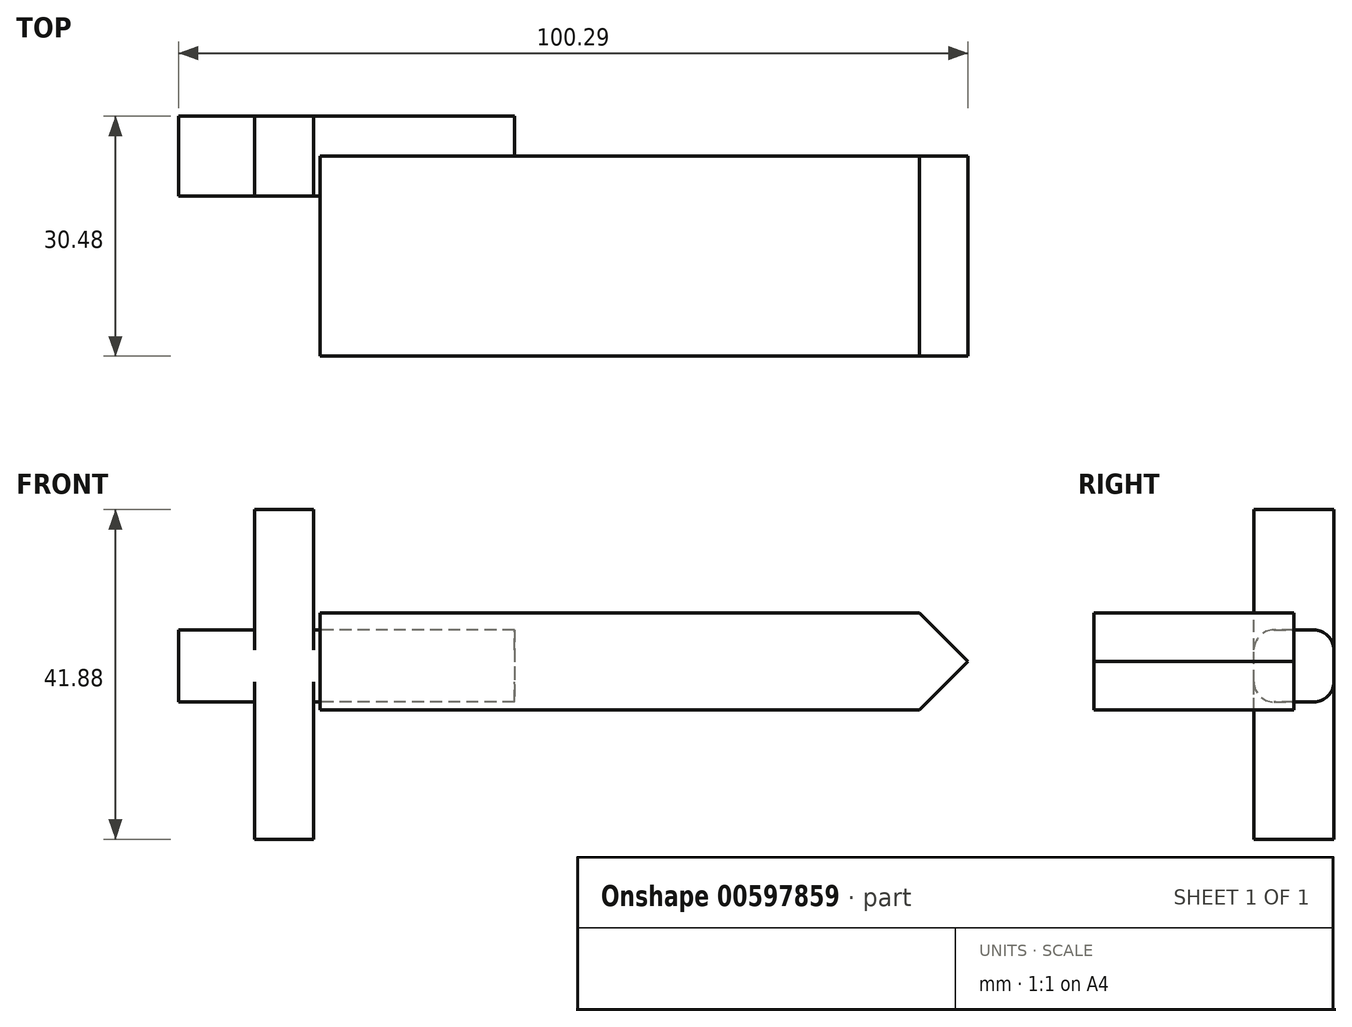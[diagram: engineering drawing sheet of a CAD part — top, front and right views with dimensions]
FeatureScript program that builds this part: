
annotation { "Feature Type Name" : "Feature", "Feature Type Description" : "" }
export const myFeature = defineFeature(function(context is Context, id is Id, definition is map)
    precondition{}
    {
        {
            var Q0;
            Q0=qCreatedBy(makeId("Front.planeOp"),FACE);
            var sketch = newSketch(context, id + "F0", { "sketchPlane" : qUnion([Q0])});
            skLineSegment(sketch, "E0.bottom", {"start": v(-28.06, 29.4) * mm, "end": v(-94.64, 29.4) * mm});
            skLineSegment(sketch, "E0.top", {"start": v(-28.06, 38.53) * mm, "end": v(-94.64, 38.53) * mm});
            skLineSegment(sketch, "E0.left", {"start": v(-28.06, 29.4) * mm, "end": v(-28.06, 38.53) * mm});
            skLineSegment(sketch, "E0.right", {"start": v(-94.64, 29.4) * mm, "end": v(-94.64, 38.53) * mm});
            skPoint(sketch, "E0.middle", {"position": v(-61.35, 33.96) * mm});
            skLineSegment(sketch, "E1.bottom", {"start": v(-84.98, 11.95) * mm, "end": v(-77.46, 11.95) * mm});
            skLineSegment(sketch, "E1.top", {"start": v(-84.98, 53.83) * mm, "end": v(-77.46, 53.83) * mm});
            skLineSegment(sketch, "E1.left", {"start": v(-84.98, 11.95) * mm, "end": v(-84.98, 53.83) * mm});
            skLineSegment(sketch, "E1.right", {"start": v(-77.46, 11.95) * mm, "end": v(-77.46, 53.83) * mm});
            skPoint(sketch, "E1.middle", {"position": v(-81.22, 32.9) * mm});
            skLineSegment(sketch, "E2.bottom", {"start": v(-51.95, 50.34) * mm, "end": v(9.53, 50.34) * mm});
            skLineSegment(sketch, "E2.top", {"start": v(-51.95, 20.8) * mm, "end": v(9.53, 20.8) * mm});
            skLineSegment(sketch, "E2.left", {"start": v(-51.95, 50.34) * mm, "end": v(-51.95, 20.8) * mm});
            skLineSegment(sketch, "E2.right", {"start": v(9.53, 50.34) * mm, "end": v(9.53, 20.8) * mm});
            skSolve(sketch);
        }
        {
            var Q0;
            {var subQ0=sQuery(id+"F0.wireOp",EDGE,"E2.left");var subQ1=sQuery(id+"F0.wireOp",EDGE,"E0.bottom");var subQ2=makeQuery(id+"F0.imprint","INTERSECT",VERTEX,{"derivedFrom":[subQ1,subQ0]});Q0=makeQuery(id+"F0.imprint","IMPRINT",FACE,{"disambiguationData":[TD([[makeQuery(id+"F0.imprint","IMPRINT",EDGE,{"disambiguationData":[TD([[subQ2,-1.0]])],"derivedFrom":subQ1}),-1.0]])]});}
            var Q1;
            {var subQ0=sQuery(id+"F0.wireOp",EDGE,"E0.right");Q1=makeQuery(id+"F0.imprint","IMPRINT",FACE,{"disambiguationData":[TD([[makeQuery(id+"F0.imprint","IMPRINT",EDGE,{"derivedFrom":subQ0}),-1.0]])]});}
            var Q2;
            {var subQ5=sQuery(id+"F0.wireOp",EDGE,"E1.top");Q2=makeQuery(id+"F0.imprint","IMPRINT",FACE,{"disambiguationData":[TD([[makeQuery(id+"F0.imprint","IMPRINT",EDGE,{"derivedFrom":subQ5}),-1.0]])]});}
            var Q3;
            {var subQ0=sQuery(id+"F0.wireOp",EDGE,"E1.right");var subQ1=sQuery(id+"F0.wireOp",EDGE,"E0.bottom");var subQ2=makeQuery(id+"F0.imprint","INTERSECT",VERTEX,{"derivedFrom":[subQ1,subQ0]});Q3=makeQuery(id+"F0.imprint","IMPRINT",FACE,{"disambiguationData":[TD([[makeQuery(id+"F0.imprint","IMPRINT",EDGE,{"disambiguationData":[TD([[subQ2,-1.0]])],"derivedFrom":subQ1}),-1.0]])]});}
            var Q4;
            {var subQ5=sQuery(id+"F0.wireOp",EDGE,"E1.bottom");Q4=makeQuery(id+"F0.imprint","IMPRINT",FACE,{"disambiguationData":[TD([[makeQuery(id+"F0.imprint","IMPRINT",EDGE,{"derivedFrom":subQ5}),1.0]])]});}
            extrude(context, id + "F1", {"entities" : qUnion([Q0, Q1, Q2, Q3, Q4]), "endBound" : BoundingType.SYMMETRIC, "depth" : 10.16 * mm, "offsetDistance" : 25.4 * mm});
        }
        {
            var Q0;
            {var subQ0=sQuery(id+"F0.wireOp",EDGE,"E0.top");Q0=makeQuery(id+"F1.opExtrude","CAP_EDGE",EDGE,{"disambiguationData":[OSD([subQ0]),TDD([makeQuery(id+"F0.imprint","IMPRINT",EDGE,{"disambiguationData":[TD([[makeQuery(id+"F0.imprint","INTERSECT",VERTEX,{"derivedFrom":[subQ0,sQuery(id+"F0.wireOp",EDGE,"E2.left")]}),-1.0]])],"derivedFrom":subQ0})])],"isStart":false});}
            var Q1;
            {var subQ0=sQuery(id+"F0.wireOp",EDGE,"E0.top");Q1=makeQuery(id+"F1.opExtrude","CAP_EDGE",EDGE,{"disambiguationData":[OSD([subQ0]),TDD([makeQuery(id+"F0.imprint","IMPRINT",EDGE,{"disambiguationData":[TD([[makeQuery(id+"F0.imprint","INTERSECT",VERTEX,{"derivedFrom":[subQ0,sQuery(id+"F0.wireOp",EDGE,"E0.right")]}),1.0]])],"derivedFrom":subQ0})])],"isStart":false});}
            fillet(context, id + "F2", {"entities" : qUnion([Q0, Q1]), "radius" : 2.54 * mm, "tangentPropagation" : true, "allowEdgeOverflow" : false});
        }
        {
            var Q0;
            {var subQ0=sQuery(id+"F0.wireOp",EDGE,"E0.bottom");Q0=makeQuery(id+"F1.opExtrude","CAP_EDGE",EDGE,{"disambiguationData":[OSD([subQ0]),TDD([makeQuery(id+"F0.imprint","IMPRINT",EDGE,{"disambiguationData":[TD([[makeQuery(id+"F0.imprint","INTERSECT",VERTEX,{"derivedFrom":[subQ0,sQuery(id+"F0.wireOp",EDGE,"E2.left")]}),-1.0]])],"derivedFrom":subQ0})])],"isStart":false});}
            var Q1;
            {var subQ0=sQuery(id+"F0.wireOp",EDGE,"E0.bottom");Q1=makeQuery(id+"F1.opExtrude","CAP_EDGE",EDGE,{"disambiguationData":[OSD([subQ0]),TDD([makeQuery(id+"F0.imprint","IMPRINT",EDGE,{"disambiguationData":[TD([[makeQuery(id+"F0.imprint","INTERSECT",VERTEX,{"derivedFrom":[subQ0,sQuery(id+"F0.wireOp",EDGE,"E0.right")]}),1.0]])],"derivedFrom":subQ0})])],"isStart":false});}
            var Q2;
            {var subQ0=sQuery(id+"F0.wireOp",EDGE,"E0.bottom");Q2=makeQuery(id+"F1.opExtrude","CAP_EDGE",EDGE,{"disambiguationData":[OSD([subQ0]),TDD([makeQuery(id+"F0.imprint","IMPRINT",EDGE,{"disambiguationData":[TD([[makeQuery(id+"F0.imprint","INTERSECT",VERTEX,{"derivedFrom":[subQ0,sQuery(id+"F0.wireOp",EDGE,"E0.right")]}),1.0]])],"derivedFrom":subQ0})])],"isStart":true});}
            var Q3;
            {var subQ0=sQuery(id+"F0.wireOp",EDGE,"E0.bottom");Q3=makeQuery(id+"F1.opExtrude","CAP_EDGE",EDGE,{"disambiguationData":[OSD([subQ0]),TDD([makeQuery(id+"F0.imprint","IMPRINT",EDGE,{"disambiguationData":[TD([[makeQuery(id+"F0.imprint","INTERSECT",VERTEX,{"derivedFrom":[subQ0,sQuery(id+"F0.wireOp",EDGE,"E2.left")]}),-1.0]])],"derivedFrom":subQ0})])],"isStart":true});}
            var Q4;
            {var subQ0=sQuery(id+"F0.wireOp",EDGE,"E0.top");Q4=makeQuery(id+"F1.opExtrude","CAP_EDGE",EDGE,{"disambiguationData":[OSD([subQ0]),TDD([makeQuery(id+"F0.imprint","IMPRINT",EDGE,{"disambiguationData":[TD([[makeQuery(id+"F0.imprint","INTERSECT",VERTEX,{"derivedFrom":[subQ0,sQuery(id+"F0.wireOp",EDGE,"E2.left")]}),-1.0]])],"derivedFrom":subQ0})])],"isStart":true});}
            var Q5;
            {var subQ0=sQuery(id+"F0.wireOp",EDGE,"E0.top");Q5=makeQuery(id+"F1.opExtrude","CAP_EDGE",EDGE,{"disambiguationData":[OSD([subQ0]),TDD([makeQuery(id+"F0.imprint","IMPRINT",EDGE,{"disambiguationData":[TD([[makeQuery(id+"F0.imprint","INTERSECT",VERTEX,{"derivedFrom":[subQ0,sQuery(id+"F0.wireOp",EDGE,"E0.right")]}),1.0]])],"derivedFrom":subQ0})])],"isStart":true});}
            fillet(context, id + "F3", {"entities" : qUnion([Q0, Q1, Q2, Q3, Q4, Q5]), "radius" : 2.54 * mm, "tangentPropagation" : true, "allowEdgeOverflow" : false});
        }
        {
            var Q0;
            Q0=qCreatedBy(makeId("Front.planeOp"),FACE);
            var sketch = newSketch(context, id + "F4", { "sketchPlane" : qUnion([Q0])});
            skLineSegment(sketch, "E3.bottom", {"start": v(-76.64, 40.7) * mm, "end": v(9.67, 40.7) * mm});
            skLineSegment(sketch, "E3.top", {"start": v(-76.64, 28.41) * mm, "end": v(9.67, 28.41) * mm});
            skLineSegment(sketch, "E3.left", {"start": v(-76.64, 40.7) * mm, "end": v(-76.64, 28.41) * mm});
            skLineSegment(sketch, "E3.right", {"start": v(9.67, 40.7) * mm, "end": v(9.67, 28.41) * mm});
            skSolve(sketch);
        }
        {
            var Q0;
            Q0 = qSketchRegion(id + "F4", true);
            extrude(context, id + "F5", {"entities" : qUnion([Q0]), "operationType" : NewBodyOperationType.ADD, "depth" : 25.4 * mm, "offsetDistance" : 25.4 * mm});
        }
        {
            var Q0;
            Q0=makeQuery(id+"F5.opExtrude","SWEPT_EDGE",EDGE,{"disambiguationData":[OSD([sQuery(id+"F4.wireOp",EDGE,"E3.bottom"),sQuery(id+"F4.wireOp",EDGE,"E3.right")])]});
            var Q1;
            Q1=makeQuery(id+"F5.opExtrude","SWEPT_EDGE",EDGE,{"disambiguationData":[OSD([sQuery(id+"F4.wireOp",EDGE,"E3.top"),sQuery(id+"F4.wireOp",EDGE,"E3.right")])]});
            chamfer(context, id + "F6", {"entities" : qUnion([Q0, Q1]), "width" : 10.16 * mm, "tangentPropagation" : true});
        }
    });
